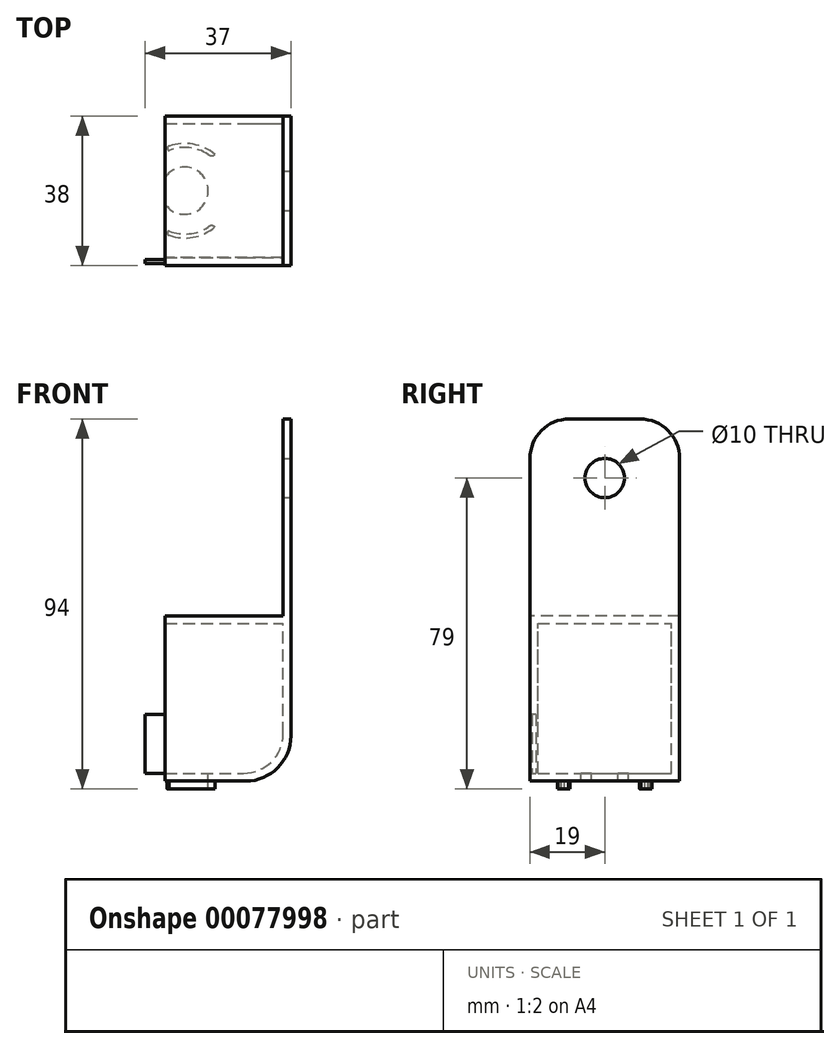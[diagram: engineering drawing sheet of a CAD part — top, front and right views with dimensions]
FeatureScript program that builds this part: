
annotation { "Feature Type Name" : "Feature", "Feature Type Description" : "" }
export const myFeature = defineFeature(function(context is Context, id is Id, definition is map)
    precondition{}
    {
        {
            var Q0;
            Q0=qCreatedBy(makeId("Front.planeOp"),FACE);
            var sketch = newSketch(context, id + "F0", { "sketchPlane" : qUnion([Q0])});
            skLineSegment(sketch, "E0", {"start": v(0, 0) * mm, "end": v(20, 0) * mm});
            skLineSegment(sketch, "E1", {"start": v(30, 10) * mm, "end": v(30, 90) * mm});
            skLineSegment(sketch, "E2.0", {"start": v(32, 9.5) * mm, "end": v(32, 90) * mm});
            skLineSegment(sketch, "E2.1", {"start": v(0, -2) * mm, "end": v(20.5, -2) * mm});
            skLineSegment(sketch, "E3", {"start": v(32, 90) * mm, "end": v(30, 90) * mm});
            skPoint(sketch, "E4.visualSharp", {"position": v(30, 0) * mm});
            skArc(sketch, "E4.filletArc", {"start": v(20, 0) * mm, "mid": v(27.07, 2.93) * mm, "end": v(30, 10) * mm});
            skPoint(sketch, "E5.visualSharp", {"position": v(32, -2) * mm});
            skArc(sketch, "E5.filletArc", {"start": v(20.5, -2) * mm, "mid": v(28.63, 1.37) * mm, "end": v(32, 9.5) * mm});
            skLineSegment(sketch, "E6", {"start": v(0, 0) * mm, "end": v(0, -2) * mm});
            skSolve(sketch);
        }
        {
            var Q0;
            Q0=qSketchRegion(id+"F0",true);
            extrude(context, id + "F1", {"entities" : qUnion([Q0]), "depth" : 38 * mm});
        }
        {
            var Q0;
            Q0=makeQuery(id+"F1.opExtrude","SWEPT_FACE",FACE,{"disambiguationData":[OSD([sQuery(id+"F0.wireOp",EDGE,"E0"),sQuery(id+"F0.wireOp",EDGE,"3ad7c5e5-9fda-4a11-b3fd-82a6be3e3b302.MirrorCS")])]});
            var sketch = newSketch(context, id + "F2", { "sketchPlane" : qUnion([Q0])});
            skLineSegment(sketch, "E7", {"start": v(0, 0) * mm, "end": v(0, -19) * mm, "construction": true});
            skCircle(sketch, "E8", {"center": v(5, -19) * mm, "radius": 6 * mm});
            skLineSegment(sketch, "E9", {"start": v(0, -19) * mm, "end": v(5, -19) * mm, "construction": true});
            skSolve(sketch);
        }
        {
            var Q0;
            Q0=sQuery(id+"F2.wireOp",VERTEX,"E8.center");
            var Q1;
            Q1=makeQuery(id+"F1.opExtrude","SWEPT_BODY",BODY,{"disambiguationData":[OSD([sQuery(id+"F0.wireOp",EDGE,"E0"),sQuery(id+"F0.wireOp",EDGE,"E1"),sQuery(id+"F0.wireOp",EDGE,"E2.0"),sQuery(id+"F0.wireOp",EDGE,"E2.1"),sQuery(id+"F0.wireOp",EDGE,"E3"),sQuery(id+"F0.wireOp",EDGE,"E4.filletArc"),sQuery(id+"F0.wireOp",EDGE,"E5.filletArc"),sQuery(id+"F0.wireOp",EDGE,"3ad7c5e5-9fda-4a11-b3fd-82a6be3e3b300.MirrorCS"),sQuery(id+"F0.wireOp",EDGE,"3ad7c5e5-9fda-4a11-b3fd-82a6be3e3b302.MirrorCS"),sQuery(id+"F0.wireOp",EDGE,"3ad7c5e5-9fda-4a11-b3fd-82a6be3e3b303.MirrorCS"),sQuery(id+"F0.wireOp",EDGE,"3ad7c5e5-9fda-4a11-b3fd-82a6be3e3b304.MirrorCS"),sQuery(id+"F0.wireOp",EDGE,"3ad7c5e5-9fda-4a11-b3fd-82a6be3e3b305.MirrorCS"),sQuery(id+"F0.wireOp",EDGE,"3ad7c5e5-9fda-4a11-b3fd-82a6be3e3b306.MirrorCS"),sQuery(id+"F0.wireOp",EDGE,"3ad7c5e5-9fda-4a11-b3fd-82a6be3e3b308.MirrorCS")])]});
            hole(context, id + "F3", {"style" : HoleStyle.SIMPLE, "holeDiameter" : 12 * mm, "endStyle" : HoleEndStyle.THROUGH, "locations" : qUnion([Q0]), "scope" : qUnion([Q1])});
        }
        {
            var Q0;
            Q0=makeQuery(id+"F1.opExtrude","SWEPT_FACE",FACE,{"disambiguationData":[OSD([sQuery(id+"F0.wireOp",EDGE,"E2.1"),sQuery(id+"F0.wireOp",EDGE,"3ad7c5e5-9fda-4a11-b3fd-82a6be3e3b303.MirrorCS")])]});
            var sketch = newSketch(context, id + "F4", { "sketchPlane" : qUnion([Q0])});
            skCircle(sketch, "E10", {"center": v(5, 19) * mm, "radius": 11 * mm, "construction": true});
            skCircle(sketch, "E11", {"center": v(5, 19) * mm, "radius": 12 * mm, "construction": true});
            skLineSegment(sketch, "E12", {"start": v(5, 14.02) * mm, "end": v(11, 14.02) * mm, "construction": true});
            skLineSegment(sketch, "E13", {"start": v(5, 14.02) * mm, "end": v(-1, 14.02) * mm, "construction": true});
            skLineSegment(sketch, "E14", {"start": v(11, 28.22) * mm, "end": v(12.68, 28.22) * mm, "construction": true});
            skLineSegment(sketch, "E15", {"start": v(11, 9.78) * mm, "end": v(12.68, 9.78) * mm, "construction": true});
            skArc(sketch, "E16", {"start": v(1, 8.75) * mm, "mid": v(6.12, 8.06) * mm, "end": v(11, 9.78) * mm});
            skArc(sketch, "E17", {"start": v(1, 7.69) * mm, "mid": v(7.12, 7.19) * mm, "end": v(12.68, 9.78) * mm});
            skArc(sketch, "E18.trimOffspring", {"start": v(11, 28.22) * mm, "mid": v(6.12, 29.94) * mm, "end": v(1, 29.25) * mm});
            skArc(sketch, "E19", {"start": v(12.68, 9.78) * mm, "mid": v(11.84, 10.12) * mm, "end": v(11, 9.78) * mm});
            skArc(sketch, "E20", {"start": v(11, 28.22) * mm, "mid": v(11.84, 27.88) * mm, "end": v(12.68, 28.22) * mm});
            skLineSegment(sketch, "E21", {"start": v(1, 30.98) * mm, "end": v(0, 30.98) * mm, "construction": true});
            skLineSegment(sketch, "E22", {"start": v(1, 30.98) * mm, "end": v(1, 6.66) * mm, "construction": true});
            skArc(sketch, "E23", {"start": v(12.68, 28.22) * mm, "mid": v(7.12, 30.81) * mm, "end": v(1, 30.31) * mm});
            skArc(sketch, "E24", {"start": v(1, 30.31) * mm, "mid": v(0.58, 29.78) * mm, "end": v(1, 29.25) * mm});
            skArc(sketch, "E25", {"start": v(1, 8.75) * mm, "mid": v(0.58, 8.22) * mm, "end": v(1, 7.69) * mm});
            skSolve(sketch);
        }
        {
            var Q0;
            Q0=makeQuery(id+"F4.imprint","IMPRINT",FACE,{"disambiguationData":[TD([[makeQuery(id+"F4.imprint","IMPRINT",EDGE,{"derivedFrom":sQuery(id+"F4.wireOp",EDGE,"E18.trimOffspring")}),-1.0]])]});
            var Q1;
            Q1=makeQuery(id+"F4.imprint","IMPRINT",FACE,{"disambiguationData":[TD([[makeQuery(id+"F4.imprint","IMPRINT",EDGE,{"derivedFrom":sQuery(id+"F4.wireOp",EDGE,"E16")}),-1.0]])]});
            extrude(context, id + "F5", {"entities" : qUnion([Q0, Q1]), "operationType" : NewBodyOperationType.ADD, "depth" : 2 * mm});
        }
        {
            var Q0;
            Q0=makeQuery(id+"F1.opExtrude","CAP_EDGE",EDGE,{"disambiguationData":[OSD([sQuery(id+"F0.wireOp",EDGE,"3ad7c5e5-9fda-4a11-b3fd-82a6be3e3b300.MirrorCS")])],"isStart":false});
            var Q1;
            Q1=makeQuery(id+"F1.opExtrude","CAP_EDGE",EDGE,{"disambiguationData":[OSD([sQuery(id+"F0.wireOp",EDGE,"E3")])],"isStart":false});
            var Q2;
            Q2=makeQuery(id+"F1.opExtrude","CAP_EDGE",EDGE,{"disambiguationData":[OSD([sQuery(id+"F0.wireOp",EDGE,"3ad7c5e5-9fda-4a11-b3fd-82a6be3e3b300.MirrorCS")])],"isStart":true});
            var Q3;
            Q3=makeQuery(id+"F1.opExtrude","CAP_EDGE",EDGE,{"disambiguationData":[OSD([sQuery(id+"F0.wireOp",EDGE,"E3")])],"isStart":true});
            fillet(context, id + "F6", {"entities" : qUnion([Q0, Q1, Q2, Q3]), "radius" : 10 * mm, "tangentPropagation" : true, "allowEdgeOverflow" : false});
        }
        {
            var Q0;
            Q0=makeQuery(id+"F1.opExtrude","SWEPT_FACE",FACE,{"disambiguationData":[OSD([sQuery(id+"F0.wireOp",EDGE,"E2.0")])]});
            var sketch = newSketch(context, id + "F7", { "sketchPlane" : qUnion([Q0])});
            skLineSegment(sketch, "E26", {"start": v(-19, 75) * mm, "end": v(-19, 90) * mm, "construction": true});
            skCircle(sketch, "E27", {"center": v(-19, 75) * mm, "radius": 5 * mm});
            skSolve(sketch);
        }
        {
            var Q0;
            Q0=sQuery(id+"F7.wireOp",VERTEX,"E26.start");
            var Q1;
            Q1=makeQuery(id+"F1.opExtrude","SWEPT_BODY",BODY,{"disambiguationData":[OSD([sQuery(id+"F0.wireOp",EDGE,"E0"),sQuery(id+"F0.wireOp",EDGE,"E1"),sQuery(id+"F0.wireOp",EDGE,"E2.0"),sQuery(id+"F0.wireOp",EDGE,"E2.1"),sQuery(id+"F0.wireOp",EDGE,"E3"),sQuery(id+"F0.wireOp",EDGE,"E4.filletArc"),sQuery(id+"F0.wireOp",EDGE,"E5.filletArc"),sQuery(id+"F0.wireOp",EDGE,"3ad7c5e5-9fda-4a11-b3fd-82a6be3e3b300.MirrorCS"),sQuery(id+"F0.wireOp",EDGE,"3ad7c5e5-9fda-4a11-b3fd-82a6be3e3b302.MirrorCS"),sQuery(id+"F0.wireOp",EDGE,"3ad7c5e5-9fda-4a11-b3fd-82a6be3e3b303.MirrorCS"),sQuery(id+"F0.wireOp",EDGE,"3ad7c5e5-9fda-4a11-b3fd-82a6be3e3b304.MirrorCS"),sQuery(id+"F0.wireOp",EDGE,"3ad7c5e5-9fda-4a11-b3fd-82a6be3e3b305.MirrorCS"),sQuery(id+"F0.wireOp",EDGE,"3ad7c5e5-9fda-4a11-b3fd-82a6be3e3b306.MirrorCS"),sQuery(id+"F0.wireOp",EDGE,"3ad7c5e5-9fda-4a11-b3fd-82a6be3e3b308.MirrorCS")])]});
            hole(context, id + "F8", {"style" : HoleStyle.SIMPLE, "holeDiameter" : 10 * mm, "endStyle" : HoleEndStyle.THROUGH, "locations" : qUnion([Q0]), "scope" : qUnion([Q1])});
        }
        {
            var Q0;
            Q0=makeQuery(id+"F1.opExtrude","CAP_FACE",FACE,{"disambiguationData":[OSD([sQuery(id+"F0.wireOp",EDGE,"E0"),sQuery(id+"F0.wireOp",EDGE,"E1"),sQuery(id+"F0.wireOp",EDGE,"E2.0"),sQuery(id+"F0.wireOp",EDGE,"E2.1"),sQuery(id+"F0.wireOp",EDGE,"E3"),sQuery(id+"F0.wireOp",EDGE,"E4.filletArc"),sQuery(id+"F0.wireOp",EDGE,"E5.filletArc"),sQuery(id+"F0.wireOp",EDGE,"E6")])],"isStart":false});
            var sketch = newSketch(context, id + "F9", { "sketchPlane" : qUnion([Q0])});
            skLineSegment(sketch, "E28", {"start": v(0, 0) * mm, "end": v(0, 40) * mm});
            skLineSegment(sketch, "E29", {"start": v(0, 40) * mm, "end": v(30, 40) * mm});
            skLineSegment(sketch, "E30", {"start": v(0, 0) * mm, "end": v(20, 0) * mm});
            skLineSegment(sketch, "E31", {"start": v(30, 40) * mm, "end": v(30, 10) * mm});
            skPoint(sketch, "E32.visualSharp", {"position": v(30, 0) * mm});
            skArc(sketch, "E32.filletArc", {"start": v(20, 0) * mm, "mid": v(27.07, 2.93) * mm, "end": v(30, 10) * mm});
            skSolve(sketch);
        }
        {
            var Q0;
            Q0=qSketchRegion(id+"F9",true);
            extrude(context, id + "F10", {"entities" : qUnion([Q0]), "oppositeDirection" : true, "depth" : 2 * mm});
        }
        {
            var Q0;
            Q0=makeQuery(id+"F1.opExtrude","CAP_FACE",FACE,{"disambiguationData":[OSD([sQuery(id+"F0.wireOp",EDGE,"E0"),sQuery(id+"F0.wireOp",EDGE,"E1"),sQuery(id+"F0.wireOp",EDGE,"E2.0"),sQuery(id+"F0.wireOp",EDGE,"E2.1"),sQuery(id+"F0.wireOp",EDGE,"E3"),sQuery(id+"F0.wireOp",EDGE,"E4.filletArc"),sQuery(id+"F0.wireOp",EDGE,"E5.filletArc"),sQuery(id+"F0.wireOp",EDGE,"E6")])],"isStart":true});
            var sketch = newSketch(context, id + "F11", { "sketchPlane" : qUnion([Q0])});
            skLineSegment(sketch, "E33", {"start": v(0, 0) * mm, "end": v(0, 40) * mm});
            skLineSegment(sketch, "E34", {"start": v(0, 40) * mm, "end": v(-30, 40) * mm});
            skLineSegment(sketch, "E35", {"start": v(-30, 40) * mm, "end": v(-30, 10) * mm});
            skLineSegment(sketch, "E36", {"start": v(-20, 0) * mm, "end": v(0, 0) * mm});
            skPoint(sketch, "E37.visualSharp", {"position": v(-30, 0) * mm});
            skArc(sketch, "E37.filletArc", {"start": v(-30, 10) * mm, "mid": v(-27.07, 2.93) * mm, "end": v(-20, 0) * mm});
            skSolve(sketch);
        }
        {
            var Q0;
            Q0=qSketchRegion(id+"F11",true);
            extrude(context, id + "F12", {"entities" : qUnion([Q0]), "oppositeDirection" : true, "depth" : 2 * mm});
        }
        {
            var Q0;
            Q0=makeQuery(id+"F1.opExtrude","SWEPT_BODY",BODY,{"disambiguationData":[OSD([sQuery(id+"F0.wireOp",EDGE,"E0"),sQuery(id+"F0.wireOp",EDGE,"E1"),sQuery(id+"F0.wireOp",EDGE,"E2.0"),sQuery(id+"F0.wireOp",EDGE,"E2.1"),sQuery(id+"F0.wireOp",EDGE,"E3"),sQuery(id+"F0.wireOp",EDGE,"E4.filletArc"),sQuery(id+"F0.wireOp",EDGE,"E5.filletArc"),sQuery(id+"F0.wireOp",EDGE,"E6")])]});
            var Q1;
            Q1=makeQuery(id+"F10.opExtrude","SWEPT_BODY",BODY,{"disambiguationData":[OSD([sQuery(id+"F9.wireOp",EDGE,"E28"),sQuery(id+"F9.wireOp",EDGE,"E29"),sQuery(id+"F9.wireOp",EDGE,"E30"),sQuery(id+"F9.wireOp",EDGE,"E31"),sQuery(id+"F9.wireOp",EDGE,"E32.filletArc")])]});
            var Q2;
            Q2=makeQuery(id+"F12.opExtrude","SWEPT_BODY",BODY,{"disambiguationData":[OSD([sQuery(id+"F11.wireOp",EDGE,"E33"),sQuery(id+"F11.wireOp",EDGE,"E34"),sQuery(id+"F11.wireOp",EDGE,"E35"),sQuery(id+"F11.wireOp",EDGE,"E36"),sQuery(id+"F11.wireOp",EDGE,"E37.filletArc")])]});
            booleanBodies(context, id + "F13", {"operationType" : BooleanOperationType.UNION, "tools" : qUnion([Q0, Q1, Q2])});
        }
        {
            var Q0;
            Q0=makeQuery(id+"F12.opExtrude","SWEPT_FACE",FACE,{"disambiguationData":[OSD([sQuery(id+"F11.wireOp",EDGE,"E34")])]});
            var sketch = newSketch(context, id + "F14", { "sketchPlane" : qUnion([Q0])});
            skLineSegment(sketch, "E38", {"start": v(0, 0) * mm, "end": v(0, -38) * mm});
            skLineSegment(sketch, "E39", {"start": v(0, -38) * mm, "end": v(30, -38) * mm});
            skLineSegment(sketch, "E40", {"start": v(30, -38) * mm, "end": v(30, -2) * mm});
            skLineSegment(sketch, "E41", {"start": v(30, -2) * mm, "end": v(0, -2) * mm});
            skSolve(sketch);
        }
        {
            var Q0;
            Q0=qSketchRegion(id+"F14",true);
            var Q1;
            {var subQ2=sQuery(id+"F14.wireOp",EDGE,"E39");Q1=makeQuery(id+"F14.imprint","IMPRINT",FACE,{"disambiguationData":[TD([[makeQuery(id+"F14.imprint","IMPRINT",EDGE,{"derivedFrom":subQ2}),1.0]])]});}
            extrude(context, id + "F15", {"entities" : qUnion([Q0, Q1]), "operationType" : NewBodyOperationType.ADD, "oppositeDirection" : true, "depth" : 2 * mm});
        }
        {
            var Q0;
            {var subQ0=sQuery(id+"F0.wireOp",EDGE,"E0");var subQ2=sQuery(id+"F0.wireOp",EDGE,"E6");var subQ3=sQuery(id+"F0.wireOp",EDGE,"E5.filletArc");var subQ4=sQuery(id+"F0.wireOp",EDGE,"E4.filletArc");var subQ5=sQuery(id+"F0.wireOp",EDGE,"E3");var subQ6=sQuery(id+"F0.wireOp",EDGE,"E2.1");var subQ7=sQuery(id+"F0.wireOp",EDGE,"E2.0");var subQ8=sQuery(id+"F0.wireOp",EDGE,"E1");var subQ11=makeQuery(id+"F1.opExtrude","SWEPT_FACE",FACE,{"disambiguationData":[OSD([subQ2])]});Q0=makeQuery(id+"F15.boolean.opBoolean","MERGE",FACE,{"derivedFrom":[makeQuery(id+"F13.opBoolean","MERGE",FACE,{"derivedFrom":[makeQuery(id+"F3.hole-0.boolean.opBoolean","SPLIT",FACE,{"disambiguationData":[TD([makeQuery(id+"F1.opExtrude","CAP_FACE",FACE,{"disambiguationData":[OSD([subQ0,subQ8,subQ7,subQ6,subQ5,subQ4,subQ3,subQ2])],"isStart":true})])],"derivedFrom":subQ11}),makeQuery(id+"F12.opExtrude","SWEPT_FACE",FACE,{"disambiguationData":[OSD([sQuery(id+"F11.wireOp",EDGE,"E33")])]})]}),makeQuery(id+"F13.opBoolean","MERGE",FACE,{"derivedFrom":[makeQuery(id+"F3.hole-0.boolean.opBoolean","SPLIT",FACE,{"disambiguationData":[TD([makeQuery(id+"F1.opExtrude","CAP_FACE",FACE,{"disambiguationData":[OSD([subQ0,subQ8,subQ7,subQ6,subQ5,subQ4,subQ3,subQ2])],"isStart":false})])],"derivedFrom":subQ11}),makeQuery(id+"F10.opExtrude","SWEPT_FACE",FACE,{"disambiguationData":[OSD([sQuery(id+"F9.wireOp",EDGE,"E28")])]})]}),makeQuery(id+"F15.opExtrude","SWEPT_FACE",FACE,{"disambiguationData":[OSD([sQuery(id+"F14.wireOp",EDGE,"E38")])]})]});}
            var sketch = newSketch(context, id + "F16", { "sketchPlane" : qUnion([Q0])});
            skLineSegment(sketch, "E42", {"start": v(37, 0) * mm, "end": v(37, 15) * mm, "construction": true});
            skLineSegment(sketch, "E43", {"start": v(36.5, 15) * mm, "end": v(36.5, 0) * mm});
            skLineSegment(sketch, "E44", {"start": v(37.5, 15) * mm, "end": v(37.5, 0) * mm});
            skLineSegment(sketch, "E45", {"start": v(37.5, 0) * mm, "end": v(36.5, 0) * mm});
            skLineSegment(sketch, "E46", {"start": v(36.5, 15) * mm, "end": v(37.5, 15) * mm});
            skLineSegment(sketch, "E47", {"start": v(0, 0) * mm, "end": v(0.35, 0) * mm, "construction": true});
            skLineSegment(sketch, "E48", {"start": v(1.65, 0) * mm, "end": v(2, 0) * mm, "construction": true});
            skLineSegment(sketch, "E49", {"start": v(0.35, 15.15) * mm, "end": v(1.65, 15.15) * mm});
            skLineSegment(sketch, "E50", {"start": v(0.35, -0.15) * mm, "end": v(1.65, -0.15) * mm});
            skLineSegment(sketch, "E51", {"start": v(0.35, 15.15) * mm, "end": v(0.35, -0.15) * mm});
            skLineSegment(sketch, "E52", {"start": v(1.65, -0.15) * mm, "end": v(1.65, 15.15) * mm});
            skSolve(sketch);
        }
        {
            var Q0;
            Q0=makeQuery(id+"F16.imprint","IMPRINT",FACE,{"disambiguationData":[TD([[makeQuery(id+"F16.imprint","IMPRINT",EDGE,{"derivedFrom":sQuery(id+"F16.wireOp",EDGE,"E43")}),1.0]])]});
            extrude(context, id + "F17", {"entities" : qUnion([Q0]), "operationType" : NewBodyOperationType.ADD, "depth" : 5 * mm});
        }
    });
